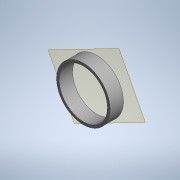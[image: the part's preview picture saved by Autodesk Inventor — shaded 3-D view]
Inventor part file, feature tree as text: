
AUTODESK INVENTOR PART (.ipt)
format: ipt  version: 2020 (Build 240168000, 168)  size: 113,152 bytes
history: native  units: mm
features: other x4, extrude x2, sketch x2, plane x1, reference x1
ambient origin geometry x8: Origin, YZ Plane, XZ Plane, XY Plane, X Axis, Y Axis, Z Axis, Center Point
bodies: 实体1 (feature_tree)
feature tree (10):
  plane  "工作平面1"
  extrude  "拉伸1"  Depth=64.0mm
  extrude  "拉伸2"  Depth=10.0mm
  sketch  "草图1"  dims[d0=80.0mm d1=64.0mm]
  reference  "参考1"
  sketch  "草图2"  dims[d2=20.0mm d3=0.0mm d4=72.0mm d5=10.0mm d6=0.0mm]
  other  "<userpath>\Desktop\ME_course_project\课设试试\shaft_try_1.iam"
  other  "shaft_try_1.iam"
  other  "轴承通盖1:1"
  other  "滚动轴承 GB/T 283 NUP 型 NUP 208 E:2"
